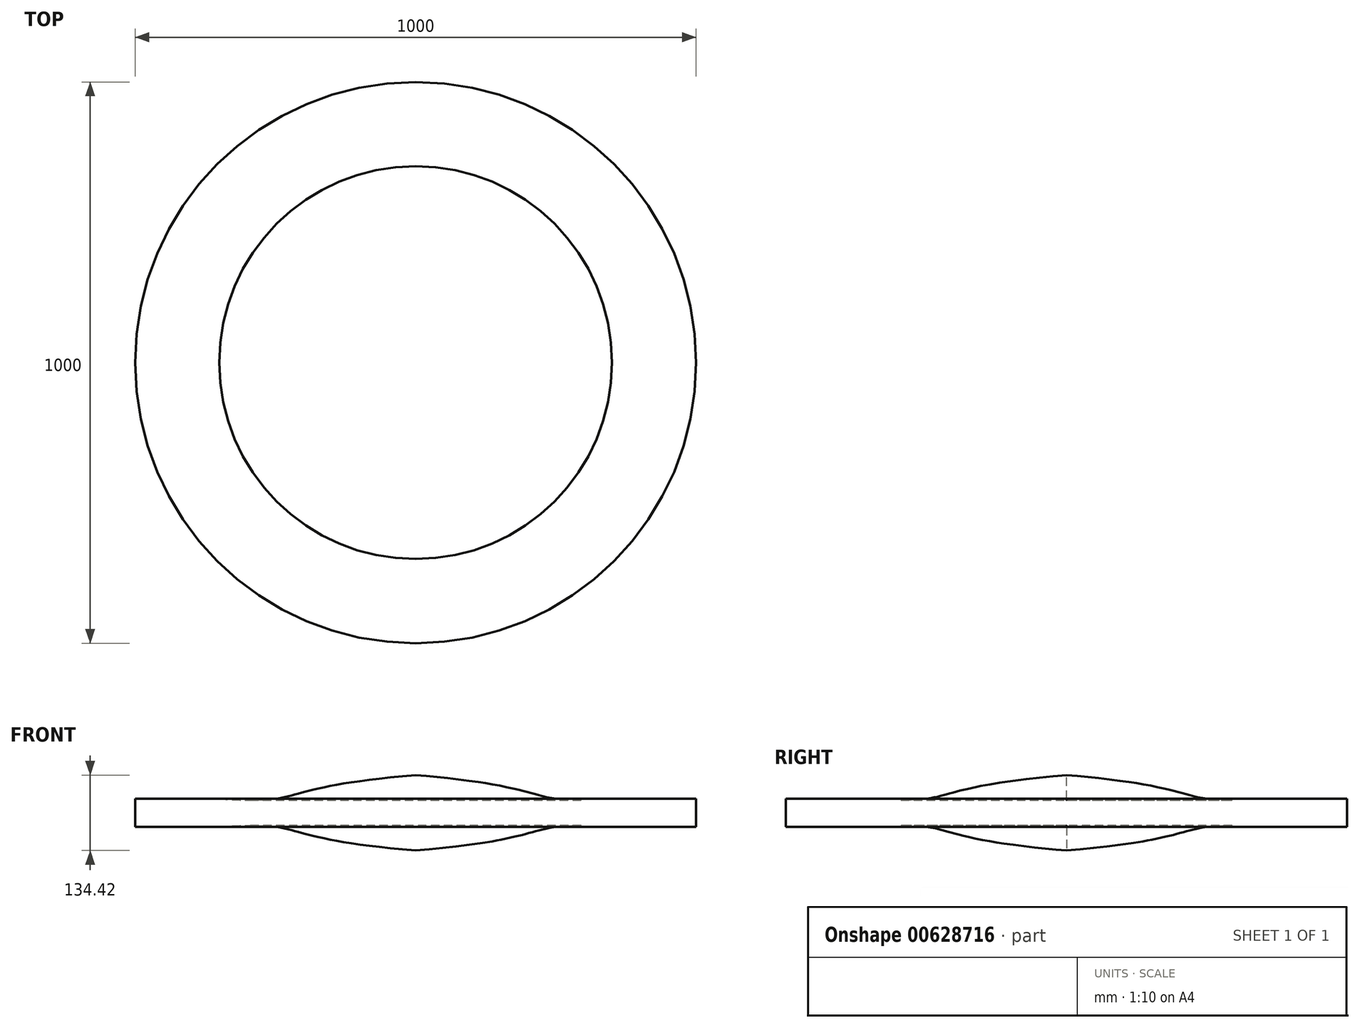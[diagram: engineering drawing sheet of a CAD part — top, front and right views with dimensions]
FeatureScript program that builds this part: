
annotation { "Feature Type Name" : "Feature", "Feature Type Description" : "" }
export const myFeature = defineFeature(function(context is Context, id is Id, definition is map)
    precondition{}
    {
        {
            var Q0;
            Q0=qCreatedBy(makeId("Front.planeOp"),FACE);
            var sketch = newSketch(context, id + "F0", { "sketchPlane" : qUnion([Q0])});
            skLineSegment(sketch, "E0", {"start": v(0, 0) * mm, "end": v(0, 134.42) * mm});
            skLineSegment(sketch, "E1", {"start": v(-500, 67.21) * mm, "end": v(0, 67.21) * mm});
            skLineSegment(sketch, "E2", {"start": v(-500, 42.21) * mm, "end": v(-350, 42.21) * mm});
            skFitSpline(sketch, "E3", {"points": [v(-350, 42.21) * mm, v(-250, 42.21) * mm, v(0, 0) * mm], "startDerivative": vector(207.5, 19.12) * mm, "endDerivative": vector(909.54, -76.76) * mm});
            skLineSegment(sketch, "E4", {"start": v(-250, 42.21) * mm, "end": v(0, 42.21) * mm, "construction": true});
            skLineSegment(sketch, "E5", {"start": v(0, 42.21) * mm, "end": v(0, 0) * mm, "construction": true});
            skLineSegment(sketch, "E6", {"start": v(-500, 67.21) * mm, "end": v(-500, 42.21) * mm});
            skFitSpline(sketch, "E7.MirrorCS", {"points": [v(-350, 92.21) * mm, v(-250, 92.21) * mm, v(0, 134.42) * mm], "startDerivative": vector(207.5, -19.12) * mm, "endDerivative": vector(909.54, 76.76) * mm});
            skLineSegment(sketch, "E8.MirrorCS", {"start": v(-500, 92.21) * mm, "end": v(-350, 92.21) * mm});
            skLineSegment(sketch, "E9.MirrorCS", {"start": v(-500, 67.21) * mm, "end": v(-500, 92.21) * mm});
            skLineSegment(sketch, "E10.MirrorCS", {"start": v(0, 92.21) * mm, "end": v(0, 134.42) * mm, "construction": true});
            skLineSegment(sketch, "E11.MirrorCS", {"start": v(-250, 92.21) * mm, "end": v(0, 92.21) * mm, "construction": true});
            skSolve(sketch);
        }
        {
            var Q0;
            Q0 = qSketchRegion(id + "F0", true);
            var Q1;
            Q1=sQuery(id+"F0.wireOp",EDGE,"E0");
            revolve(context, id + "F1", {"entities" : qUnion([Q0]), "axis" : qUnion([Q1]), "revolveType" : RevolveType.FULL});
        }
    });
